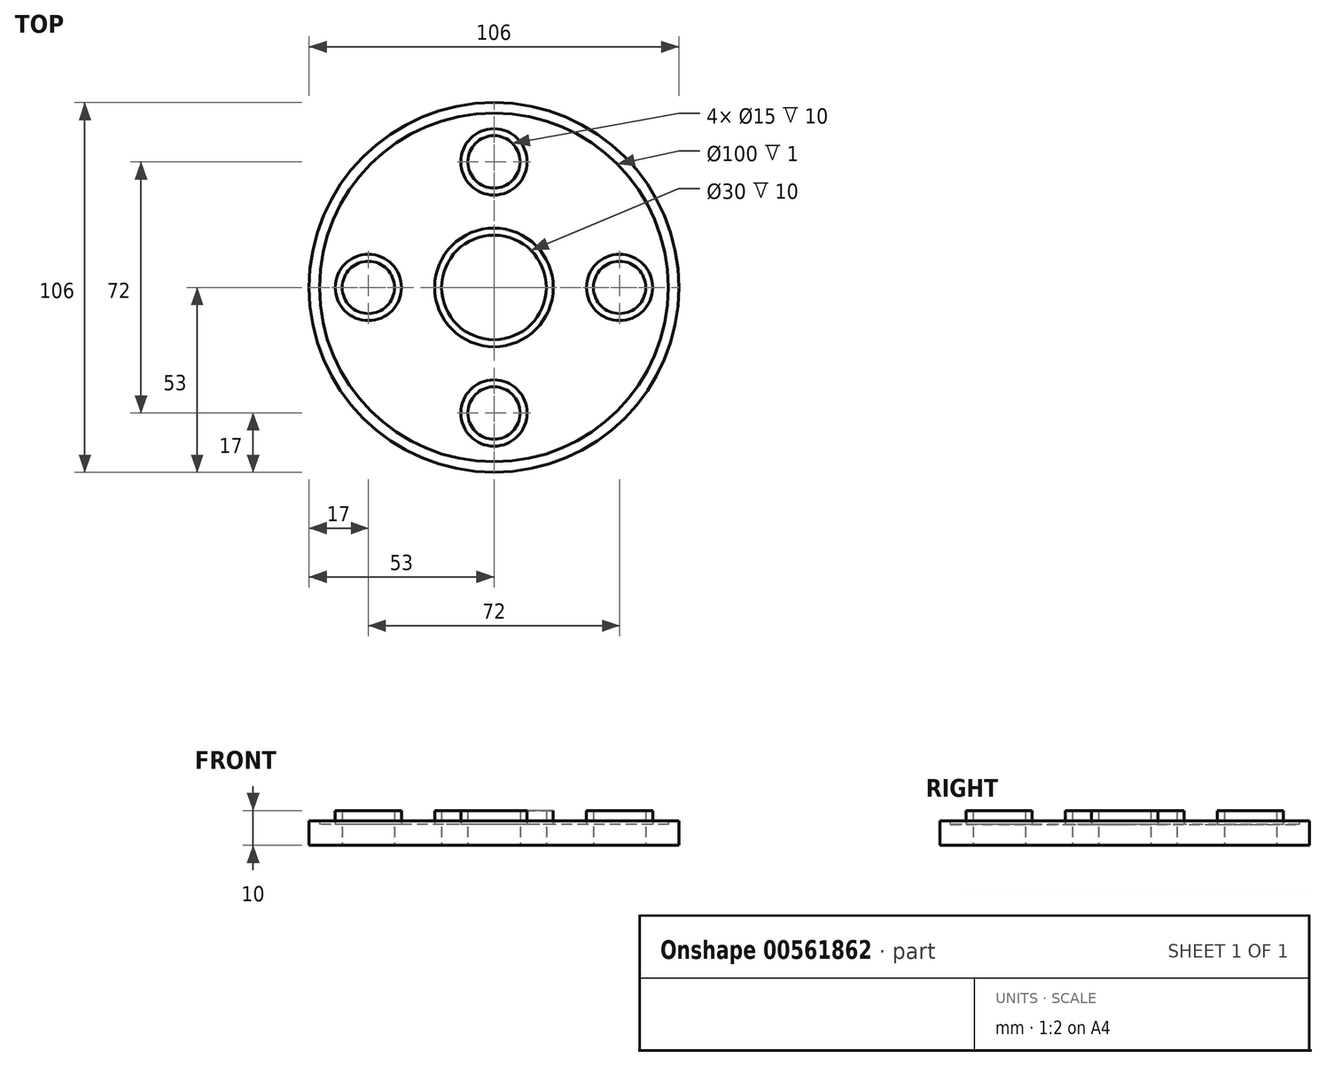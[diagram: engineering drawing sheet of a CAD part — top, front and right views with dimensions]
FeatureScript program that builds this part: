
annotation { "Feature Type Name" : "Feature", "Feature Type Description" : "" }
export const myFeature = defineFeature(function(context is Context, id is Id, definition is map)
    precondition{}
    {
        {
            var Q0;
            Q0=qCreatedBy(makeId("Top.planeOp"),FACE);
            var sketch = newSketch(context, id + "F0", { "sketchPlane" : qUnion([Q0])});
            skCircle(sketch, "E0", {"center": v(0, 0) * mm, "radius": 53 * mm});
            skCircle(sketch, "E1", {"center": v(0, 0) * mm, "radius": 50 * mm});
            skCircle(sketch, "E2", {"center": v(0, 0) * mm, "radius": 15 * mm});
            skCircle(sketch, "E3", {"center": v(0, 0) * mm, "radius": 17 * mm});
            skCircle(sketch, "E4", {"center": v(-36, 0) * mm, "radius": 7.5 * mm});
            skCircle(sketch, "E5", {"center": v(-36, 0) * mm, "radius": 9.5 * mm});
            skCircle(sketch, "E6", {"center": v(0, 36) * mm, "radius": 7.5 * mm});
            skCircle(sketch, "E7", {"center": v(36, 0) * mm, "radius": 7.5 * mm});
            skCircle(sketch, "E8", {"center": v(0, -36) * mm, "radius": 7.5 * mm});
            skCircle(sketch, "E9", {"center": v(0, -36) * mm, "radius": 9.5 * mm});
            skCircle(sketch, "E10", {"center": v(36, 0) * mm, "radius": 9.5 * mm});
            skCircle(sketch, "E11", {"center": v(0, 36) * mm, "radius": 9.5 * mm});
            skSolve(sketch);
        }
        {
            var Q0;
            Q0=makeQuery(id+"F0.imprint","IMPRINT",FACE,{"disambiguationData":[TD([[makeQuery(id+"F0.imprint","IMPRINT",EDGE,{"derivedFrom":sQuery(id+"F0.wireOp",EDGE,"E1")}),1.0]])]});
            extrude(context, id + "F1", {"entities" : qUnion([Q0]), "depth" : 6 * mm, "offsetDistance" : 25 * mm});
        }
        {
            var Q0;
            Q0=makeQuery(id+"F0.imprint","IMPRINT",FACE,{"disambiguationData":[TD([[makeQuery(id+"F0.imprint","IMPRINT",EDGE,{"derivedFrom":sQuery(id+"F0.wireOp",EDGE,"E0")}),1.0]])]});
            extrude(context, id + "F2", {"entities" : qUnion([Q0]), "operationType" : NewBodyOperationType.ADD, "depth" : 7 * mm, "offsetDistance" : 25 * mm});
        }
        {
            var Q0;
            Q0=makeQuery(id+"F0.imprint","IMPRINT",FACE,{"disambiguationData":[TD([[makeQuery(id+"F0.imprint","IMPRINT",EDGE,{"derivedFrom":sQuery(id+"F0.wireOp",EDGE,"E8")}),-1.0]])]});
            var Q1;
            Q1=makeQuery(id+"F0.imprint","IMPRINT",FACE,{"disambiguationData":[TD([[makeQuery(id+"F0.imprint","IMPRINT",EDGE,{"derivedFrom":sQuery(id+"F0.wireOp",EDGE,"E4")}),-1.0]])]});
            var Q2;
            Q2=makeQuery(id+"F0.imprint","IMPRINT",FACE,{"disambiguationData":[TD([[makeQuery(id+"F0.imprint","IMPRINT",EDGE,{"derivedFrom":sQuery(id+"F0.wireOp",EDGE,"E2")}),-1.0]])]});
            var Q3;
            Q3=makeQuery(id+"F0.imprint","IMPRINT",FACE,{"disambiguationData":[TD([[makeQuery(id+"F0.imprint","IMPRINT",EDGE,{"derivedFrom":sQuery(id+"F0.wireOp",EDGE,"E6")}),-1.0]])]});
            var Q4;
            Q4=makeQuery(id+"F0.imprint","IMPRINT",FACE,{"disambiguationData":[TD([[makeQuery(id+"F0.imprint","IMPRINT",EDGE,{"derivedFrom":sQuery(id+"F0.wireOp",EDGE,"E7")}),-1.0]])]});
            extrude(context, id + "F3", {"entities" : qUnion([Q0, Q1, Q2, Q3, Q4]), "operationType" : NewBodyOperationType.ADD, "depth" : 10 * mm, "offsetDistance" : 25 * mm});
        }
    });
